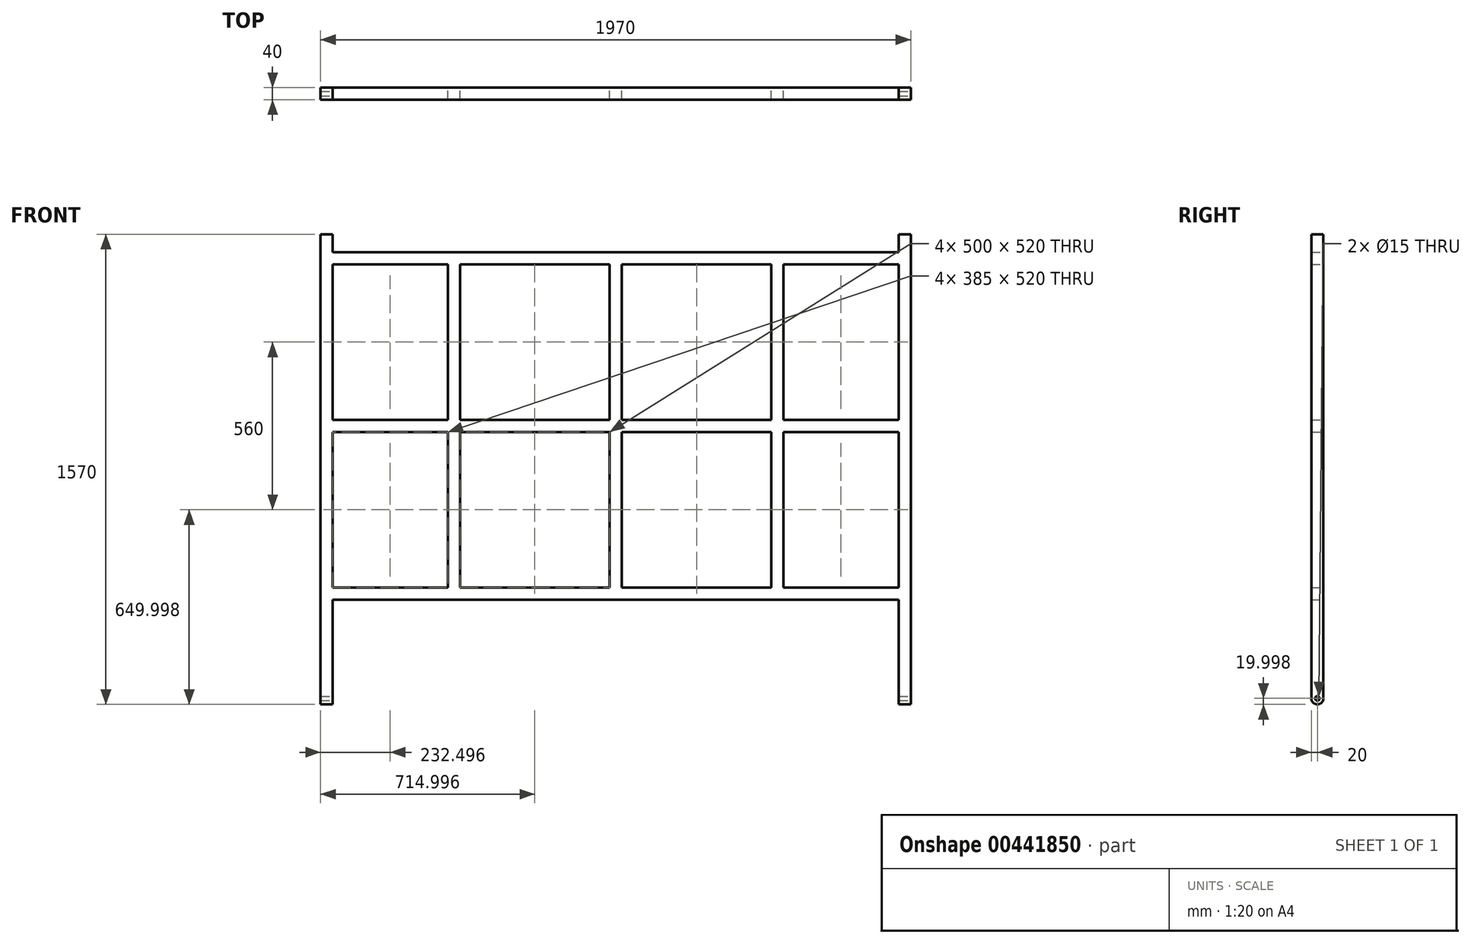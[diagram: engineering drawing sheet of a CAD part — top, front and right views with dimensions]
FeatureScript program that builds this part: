
annotation { "Feature Type Name" : "Feature", "Feature Type Description" : "" }
export const myFeature = defineFeature(function(context is Context, id is Id, definition is map)
    precondition{}
    {
        {
            var Q0;
            Q0=qCreatedBy(makeId("Front.planeOp"),FACE);
            var sketch = newSketch(context, id + "F0", { "sketchPlane" : qUnion([Q0])});
            skPoint(sketch, "E0.middle", {"position": v(0, 0) * mm});
            skLineSegment(sketch, "E1", {"start": v(-506.01, 897.1) * mm, "end": v(-506.01, -672.9) * mm});
            skLineSegment(sketch, "E2", {"start": v(-506.01, -672.9) * mm, "end": v(-466.01, -672.9) * mm});
            skLineSegment(sketch, "E3", {"start": v(-466.01, -672.9) * mm, "end": v(-466.01, -322.9) * mm});
            skLineSegment(sketch, "E4", {"start": v(-466.01, -322.9) * mm, "end": v(1423.99, -322.9) * mm});
            skLineSegment(sketch, "E5", {"start": v(1423.99, -322.9) * mm, "end": v(1423.99, -672.9) * mm});
            skLineSegment(sketch, "E6", {"start": v(1423.99, -672.9) * mm, "end": v(1463.99, -672.9) * mm});
            skLineSegment(sketch, "E7", {"start": v(1463.99, -672.9) * mm, "end": v(1463.99, 897.1) * mm});
            skLineSegment(sketch, "E8", {"start": v(1463.99, 897.1) * mm, "end": v(1423.99, 897.1) * mm});
            skLineSegment(sketch, "E9", {"start": v(1423.99, 897.1) * mm, "end": v(1423.99, 837.1) * mm});
            skLineSegment(sketch, "E10", {"start": v(1423.99, 837.1) * mm, "end": v(-466.01, 837.1) * mm});
            skLineSegment(sketch, "E11", {"start": v(-466.01, 837.1) * mm, "end": v(-466.01, 897.1) * mm});
            skLineSegment(sketch, "E12", {"start": v(-466.01, 897.1) * mm, "end": v(-506.01, 897.1) * mm});
            skLineSegment(sketch, "E13", {"start": v(-466.01, 837.1) * mm, "end": v(-466.01, -322.9) * mm});
            skLineSegment(sketch, "E14", {"start": v(1423.99, 837.1) * mm, "end": v(1423.99, -322.9) * mm});
            skLineSegment(sketch, "E15", {"start": v(-81.01, 837.1) * mm, "end": v(-81.01, -322.9) * mm});
            skLineSegment(sketch, "E16", {"start": v(-41.01, 837.1) * mm, "end": v(-41.01, -322.9) * mm});
            skLineSegment(sketch, "E17", {"start": v(458.99, 837.1) * mm, "end": v(458.99, -322.9) * mm});
            skLineSegment(sketch, "E18", {"start": v(498.99, 837.1) * mm, "end": v(498.99, -322.9) * mm});
            skLineSegment(sketch, "E19", {"start": v(1038.99, 837.1) * mm, "end": v(1038.99, -322.9) * mm});
            skLineSegment(sketch, "E20", {"start": v(-466.01, 277.1) * mm, "end": v(1423.99, 277.1) * mm});
            skLineSegment(sketch, "E21", {"start": v(-466.01, 237.1) * mm, "end": v(1423.99, 237.1) * mm});
            skLineSegment(sketch, "E22", {"start": v(-466.01, 797.1) * mm, "end": v(1423.99, 797.1) * mm});
            skLineSegment(sketch, "E23", {"start": v(-466.01, -282.9) * mm, "end": v(1423.99, -282.9) * mm});
            skLineSegment(sketch, "E24", {"start": v(998.99, 837.1) * mm, "end": v(998.99, -322.9) * mm});
            skSolve(sketch);
        }
        {
            var Q0;
            Q0 = qSketchRegion(id + "F0", true);
            var Q1;
            {var subQ0=sQuery(id+"F0.wireOp",EDGE,"E22");var subQ1=sQuery(id+"F0.wireOp",EDGE,"E15");var subQ2=makeQuery(id+"F0.imprint","INTERSECT",VERTEX,{"derivedFrom":[subQ1,subQ0]});Q1=makeQuery(id+"F0.imprint","IMPRINT",FACE,{"disambiguationData":[TD([[makeQuery(id+"F0.imprint","IMPRINT",EDGE,{"disambiguationData":[TD([[subQ2,-1.0]])],"derivedFrom":subQ1}),1.0]])]});}
            var Q2;
            {var subQ0=sQuery(id+"F0.wireOp",EDGE,"E20");var subQ1=sQuery(id+"F0.wireOp",EDGE,"E13");var subQ2=makeQuery(id+"F0.imprint","INTERSECT",VERTEX,{"derivedFrom":[subQ1,subQ0]});Q2=makeQuery(id+"F0.imprint","IMPRINT",FACE,{"disambiguationData":[TD([[makeQuery(id+"F0.imprint","IMPRINT",EDGE,{"disambiguationData":[TD([[subQ2,-1.0]])],"derivedFrom":subQ1}),1.0]])]});}
            var Q3;
            {var subQ0=sQuery(id+"F0.wireOp",EDGE,"E20");var subQ1=sQuery(id+"F0.wireOp",EDGE,"E15");var subQ2=makeQuery(id+"F0.imprint","INTERSECT",VERTEX,{"derivedFrom":[subQ1,subQ0]});Q3=makeQuery(id+"F0.imprint","IMPRINT",FACE,{"disambiguationData":[TD([[makeQuery(id+"F0.imprint","IMPRINT",EDGE,{"disambiguationData":[TD([[subQ2,-1.0]])],"derivedFrom":subQ1}),1.0]])]});}
            var Q4;
            {var subQ0=sQuery(id+"F0.wireOp",EDGE,"E21");var subQ1=sQuery(id+"F0.wireOp",EDGE,"E15");var subQ2=makeQuery(id+"F0.imprint","INTERSECT",VERTEX,{"derivedFrom":[subQ1,subQ0]});Q4=makeQuery(id+"F0.imprint","IMPRINT",FACE,{"disambiguationData":[TD([[makeQuery(id+"F0.imprint","IMPRINT",EDGE,{"disambiguationData":[TD([[subQ2,-1.0]])],"derivedFrom":subQ1}),1.0]])]});}
            var Q5;
            {var subQ0=sQuery(id+"F0.wireOp",EDGE,"E20");var subQ1=sQuery(id+"F0.wireOp",EDGE,"E16");var subQ2=makeQuery(id+"F0.imprint","INTERSECT",VERTEX,{"derivedFrom":[subQ1,subQ0]});Q5=makeQuery(id+"F0.imprint","IMPRINT",FACE,{"disambiguationData":[TD([[makeQuery(id+"F0.imprint","IMPRINT",EDGE,{"disambiguationData":[TD([[subQ2,-1.0]])],"derivedFrom":subQ1}),1.0]])]});}
            var Q6;
            {var subQ0=sQuery(id+"F0.wireOp",EDGE,"E20");var subQ1=sQuery(id+"F0.wireOp",EDGE,"E19");var subQ2=makeQuery(id+"F0.imprint","INTERSECT",VERTEX,{"derivedFrom":[subQ1,subQ0]});Q6=makeQuery(id+"F0.imprint","IMPRINT",FACE,{"disambiguationData":[TD([[makeQuery(id+"F0.imprint","IMPRINT",EDGE,{"disambiguationData":[TD([[subQ2,-1.0]])],"derivedFrom":subQ1}),1.0]])]});}
            var Q7;
            {var subQ0=sQuery(id+"F0.wireOp",EDGE,"E20");var subQ1=sQuery(id+"F0.wireOp",EDGE,"E17");var subQ2=makeQuery(id+"F0.imprint","INTERSECT",VERTEX,{"derivedFrom":[subQ1,subQ0]});Q7=makeQuery(id+"F0.imprint","IMPRINT",FACE,{"disambiguationData":[TD([[makeQuery(id+"F0.imprint","IMPRINT",EDGE,{"disambiguationData":[TD([[subQ2,-1.0]])],"derivedFrom":subQ1}),-1.0]])]});}
            var Q8;
            {var subQ0=sQuery(id+"F0.wireOp",EDGE,"E20");var subQ1=sQuery(id+"F0.wireOp",EDGE,"E17");var subQ2=makeQuery(id+"F0.imprint","INTERSECT",VERTEX,{"derivedFrom":[subQ1,subQ0]});Q8=makeQuery(id+"F0.imprint","IMPRINT",FACE,{"disambiguationData":[TD([[makeQuery(id+"F0.imprint","IMPRINT",EDGE,{"disambiguationData":[TD([[subQ2,-1.0]])],"derivedFrom":subQ1}),1.0]])]});}
            var Q9;
            {var subQ0=sQuery(id+"F0.wireOp",EDGE,"E21");var subQ1=sQuery(id+"F0.wireOp",EDGE,"E17");var subQ2=makeQuery(id+"F0.imprint","INTERSECT",VERTEX,{"derivedFrom":[subQ1,subQ0]});Q9=makeQuery(id+"F0.imprint","IMPRINT",FACE,{"disambiguationData":[TD([[makeQuery(id+"F0.imprint","IMPRINT",EDGE,{"disambiguationData":[TD([[subQ2,-1.0]])],"derivedFrom":subQ1}),1.0]])]});}
            var Q10;
            {var subQ0=sQuery(id+"F0.wireOp",EDGE,"E20");var subQ1=sQuery(id+"F0.wireOp",EDGE,"E14");var subQ2=makeQuery(id+"F0.imprint","INTERSECT",VERTEX,{"derivedFrom":[subQ1,subQ0]});Q10=makeQuery(id+"F0.imprint","IMPRINT",FACE,{"disambiguationData":[TD([[makeQuery(id+"F0.imprint","IMPRINT",EDGE,{"disambiguationData":[TD([[subQ2,-1.0]])],"derivedFrom":subQ1}),-1.0]])]});}
            var Q11;
            {var subQ0=sQuery(id+"F0.wireOp",EDGE,"E22");var subQ1=sQuery(id+"F0.wireOp",EDGE,"E17");var subQ2=makeQuery(id+"F0.imprint","INTERSECT",VERTEX,{"derivedFrom":[subQ1,subQ0]});Q11=makeQuery(id+"F0.imprint","IMPRINT",FACE,{"disambiguationData":[TD([[makeQuery(id+"F0.imprint","IMPRINT",EDGE,{"disambiguationData":[TD([[subQ2,-1.0]])],"derivedFrom":subQ1}),1.0]])]});}
            var Q12;
            {var subQ0=sQuery(id+"F0.wireOp",EDGE,"E20");var subQ1=sQuery(id+"F0.wireOp",EDGE,"E18");var subQ2=makeQuery(id+"F0.imprint","INTERSECT",VERTEX,{"derivedFrom":[subQ1,subQ0]});Q12=makeQuery(id+"F0.imprint","IMPRINT",FACE,{"disambiguationData":[TD([[makeQuery(id+"F0.imprint","IMPRINT",EDGE,{"disambiguationData":[TD([[subQ2,-1.0]])],"derivedFrom":subQ1}),1.0]])]});}
            var Q13;
            {var subQ0=sQuery(id+"F0.wireOp",EDGE,"E20");var subQ1=sQuery(id+"F0.wireOp",EDGE,"E19");var subQ2=makeQuery(id+"F0.imprint","INTERSECT",VERTEX,{"derivedFrom":[subQ1,subQ0]});Q13=makeQuery(id+"F0.imprint","IMPRINT",FACE,{"disambiguationData":[TD([[makeQuery(id+"F0.imprint","IMPRINT",EDGE,{"disambiguationData":[TD([[subQ2,-1.0]])],"derivedFrom":subQ1}),-1.0]])]});}
            var Q14;
            {var subQ0=sQuery(id+"F0.wireOp",EDGE,"E22");var subQ1=sQuery(id+"F0.wireOp",EDGE,"E19");var subQ2=makeQuery(id+"F0.imprint","INTERSECT",VERTEX,{"derivedFrom":[subQ1,subQ0]});Q14=makeQuery(id+"F0.imprint","IMPRINT",FACE,{"disambiguationData":[TD([[makeQuery(id+"F0.imprint","IMPRINT",EDGE,{"disambiguationData":[TD([[subQ2,-1.0]])],"derivedFrom":subQ1}),-1.0]])]});}
            var Q15;
            {var subQ0=sQuery(id+"F0.wireOp",EDGE,"E21");var subQ1=sQuery(id+"F0.wireOp",EDGE,"E19");var subQ2=makeQuery(id+"F0.imprint","INTERSECT",VERTEX,{"derivedFrom":[subQ1,subQ0]});Q15=makeQuery(id+"F0.imprint","IMPRINT",FACE,{"disambiguationData":[TD([[makeQuery(id+"F0.imprint","IMPRINT",EDGE,{"disambiguationData":[TD([[subQ2,-1.0]])],"derivedFrom":subQ1}),-1.0]])]});}
            extrude(context, id + "F1", {"entities" : qUnion([Q0, Q1, Q2, Q3, Q4, Q5, Q6, Q7, Q8, Q9, Q10, Q11, Q12, Q13, Q14, Q15]), "depth" : 40 * mm});
        }
        {
            var Q0;
            Q0=makeQuery(id+"F1.opExtrude","SWEPT_FACE",FACE,{"disambiguationData":[OSD([sQuery(id+"F0.wireOp",EDGE,"E7")])]});
            var sketch = newSketch(context, id + "F2", { "sketchPlane" : qUnion([Q0])});
            skCircle(sketch, "E25", {"center": v(-20, -652.9) * mm, "radius": 7.5 * mm});
            skPoint(sketch, "E25.centerSnap0", {"position": v(-20, -672.9) * mm});
            skArc(sketch, "E26", {"start": v(-40, -652.9) * mm, "mid": v(-20, -672.9) * mm, "end": v(0, -652.9) * mm});
            skLineSegment(sketch, "E27", {"start": v(-40, -672.9) * mm, "end": v(0, -672.9) * mm});
            skLineSegment(sketch, "E28", {"start": v(0, -672.9) * mm, "end": v(0, -652.9) * mm});
            skLineSegment(sketch, "E29", {"start": v(-40, -672.9) * mm, "end": v(-40, -652.9) * mm});
            skSolve(sketch);
        }
        {
            var Q0;
            Q0=makeQuery(id+"F2.imprint","IMPRINT",FACE,{"disambiguationData":[TD([[makeQuery(id+"F2.imprint","IMPRINT",EDGE,{"derivedFrom":sQuery(id+"F2.wireOp",EDGE,"E25")}),1.0]])]});
            var Q1;
            {var subQ0=sQuery(id+"F2.wireOp",EDGE,"E29");Q1=makeQuery(id+"F2.imprint","IMPRINT",FACE,{"disambiguationData":[TD([[makeQuery(id+"F2.imprint","IMPRINT",EDGE,{"derivedFrom":subQ0}),-1.0]])]});}
            var Q2;
            {var subQ0=sQuery(id+"F2.wireOp",EDGE,"E28");Q2=makeQuery(id+"F2.imprint","IMPRINT",FACE,{"disambiguationData":[TD([[makeQuery(id+"F2.imprint","IMPRINT",EDGE,{"derivedFrom":subQ0}),1.0]])]});}
            var Q3;
            Q3=makeQuery(id+"F1.opExtrude","SWEPT_FACE",FACE,{"disambiguationData":[OSD([sQuery(id+"F0.wireOp",EDGE,"E1")])]});
            extrude(context, id + "F3", {"entities" : qUnion([Q0, Q1, Q2]), "operationType" : NewBodyOperationType.REMOVE, "endBound" : BoundingType.UP_TO_SURFACE, "oppositeDirection" : true, "endBoundEntityFace" : qUnion([Q3]), "depth" : 25 * mm});
        }
    });
